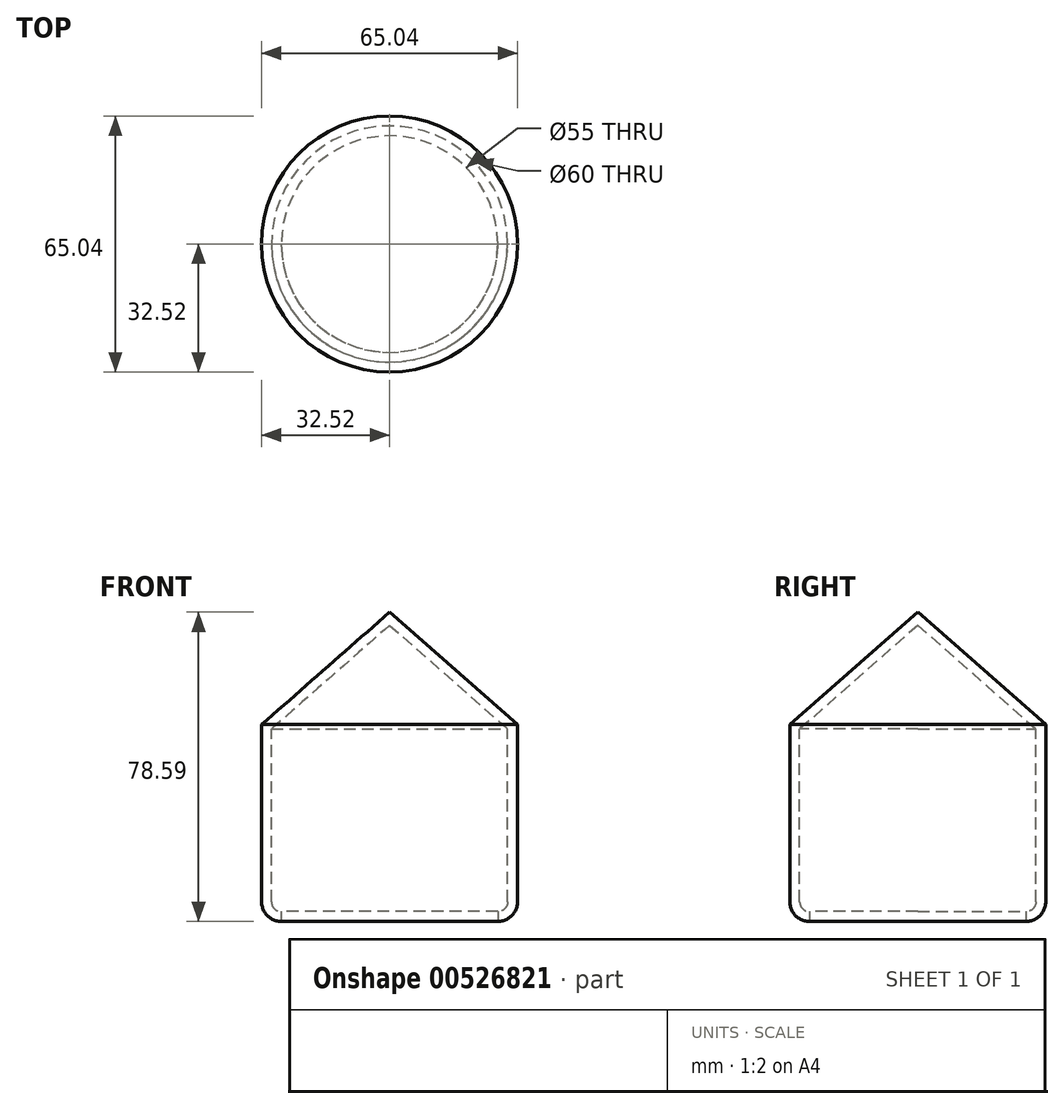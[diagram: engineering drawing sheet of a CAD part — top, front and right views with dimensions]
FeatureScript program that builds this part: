
annotation { "Feature Type Name" : "Feature", "Feature Type Description" : "" }
export const myFeature = defineFeature(function(context is Context, id is Id, definition is map)
    precondition{}
    {
        {
            var Q0;
            Q0=qCreatedBy(makeId("Front.planeOp"),FACE);
            var sketch = newSketch(context, id + "F0", { "sketchPlane" : qUnion([Q0])});
            skLineSegment(sketch, "E0", {"start": v(0, 0) * mm, "end": v(32.52, 0) * mm, "construction": true});
            skPoint(sketch, "E1.endSnap0", {"position": v(0, 0) * mm});
            skLineSegment(sketch, "E2", {"start": v(0, 28.59) * mm, "end": v(32.52, 0) * mm});
            skLineSegment(sketch, "E3", {"start": v(0, 0) * mm, "end": v(0, 28.59) * mm});
            skLineSegment(sketch, "E4", {"start": v(32.52, 0) * mm, "end": v(0, 0) * mm});
            skSolve(sketch);
        }
        {
            var Q0;
            Q0=makeQuery(id+"F0.imprint","IMPRINT",FACE,{"disambiguationData":[TD([[makeQuery(id+"F0.imprint","IMPRINT",EDGE,{"derivedFrom":sQuery(id+"F0.wireOp",EDGE,"E2")}),-1.0]])]});
            var Q1;
            Q1=sQuery(id+"F0.wireOp",EDGE,"E3");
            revolve(context, id + "F1", {"entities" : qUnion([Q0]), "axis" : qUnion([Q1]), "revolveType" : RevolveType.FULL});
        }
        {
            var Q0;
            Q0=makeQuery(id+"F1.opRevolve","SWEPT_FACE",FACE,{"disambiguationData":[OSD([sQuery(id+"F0.wireOp",EDGE,"E4")])]});
            var sketch = newSketch(context, id + "F2", { "sketchPlane" : qUnion([Q0])});
            skCircle(sketch, "E5", {"center": v(0, 0) * mm, "radius": 32.5 * mm});
            skSolve(sketch);
        }
        {
            var Q0;
            Q0 = qSketchRegion(id + "F2", true);
            extrude(context, id + "F3", {"entities" : qUnion([Q0]), "operationType" : NewBodyOperationType.ADD, "depth" : 50 * mm, "offsetDistance" : 25 * mm});
        }
        {
            var Q0;
            Q0=makeQuery(id+"F3.opExtrude","CAP_EDGE",EDGE,{"disambiguationData":[OSD([sQuery(id+"F2.wireOp",EDGE,"E5")])],"isStart":false});
            fillet(context, id + "F4", {"entities" : qUnion([Q0]), "radius" : 5 * mm, "tangentPropagation" : true, "allowEdgeOverflow" : false});
        }
        {
            var Q0;
            Q0=makeQuery(id+"F3.opExtrude","CAP_FACE",FACE,{"disambiguationData":[OSD([sQuery(id+"F2.wireOp",EDGE,"E5")])],"isStart":false});
            shell(context, id + "F5", {"entities" : qUnion([Q0]), "thickness" : 2.5 * mm});
        }
    });
